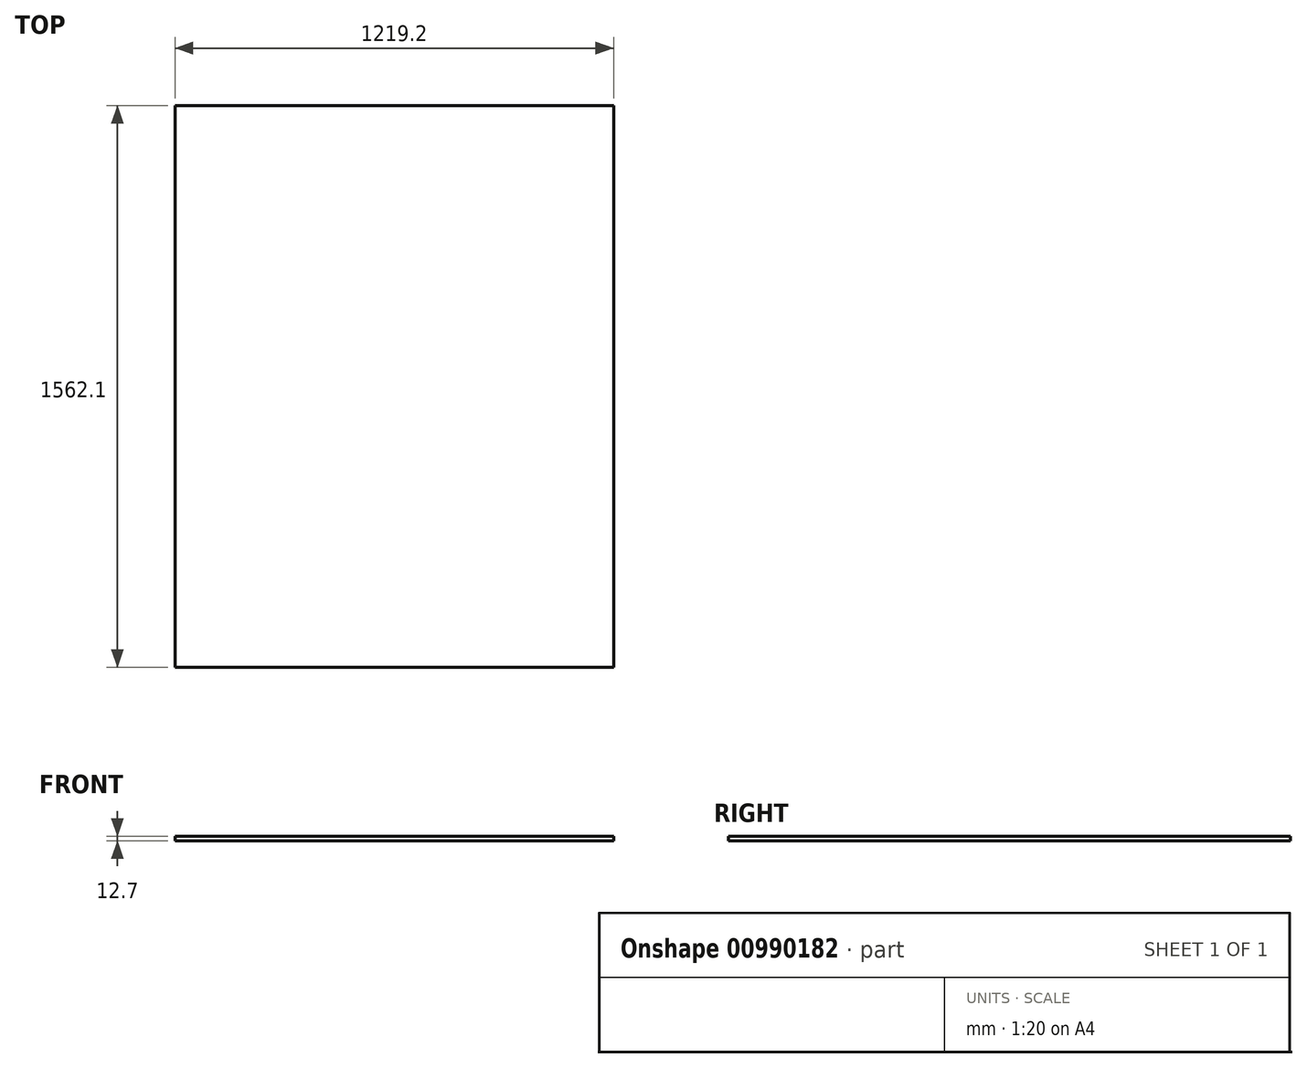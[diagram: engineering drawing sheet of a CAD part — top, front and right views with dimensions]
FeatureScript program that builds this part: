
annotation { "Feature Type Name" : "Feature", "Feature Type Description" : "" }
export const myFeature = defineFeature(function(context is Context, id is Id, definition is map)
    precondition{}
    {
        {
            var Q0;
            Q0=qCreatedBy(makeId("Top.planeOp"),FACE);
            var sketch = newSketch(context, id + "F0", { "sketchPlane" : qUnion([Q0])});
            skLineSegment(sketch, "E0.bottom", {"start": v(609.6, 781.05) * mm, "end": v(-609.6, 781.05) * mm});
            skLineSegment(sketch, "E0.top", {"start": v(609.6, -781.05) * mm, "end": v(-609.6, -781.05) * mm});
            skLineSegment(sketch, "E0.left", {"start": v(609.6, 781.05) * mm, "end": v(609.6, -781.05) * mm});
            skLineSegment(sketch, "E0.right", {"start": v(-609.6, 781.05) * mm, "end": v(-609.6, -781.05) * mm});
            skPoint(sketch, "E0.middle", {"position": v(0, 0) * mm});
            skSolve(sketch);
        }
        {
            var Q0;
            Q0=qSketchRegion(id+"F0",true);
            extrude(context, id + "F1", {"entities" : qUnion([Q0]), "depth" : 12.7 * mm, "offsetDistance" : 25.4 * mm});
        }
    });
